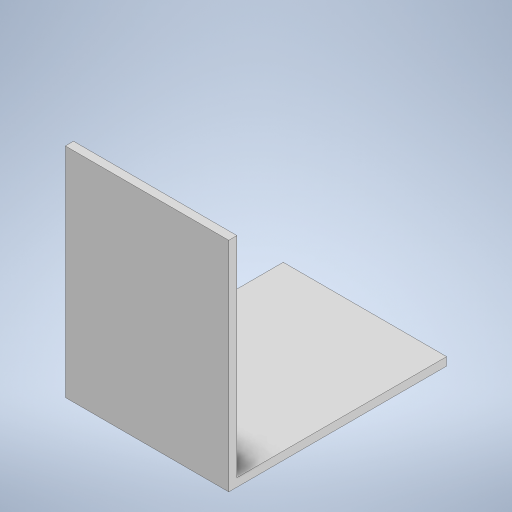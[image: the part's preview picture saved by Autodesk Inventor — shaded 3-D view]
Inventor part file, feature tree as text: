
AUTODESK INVENTOR PART (.ipt)
format: ipt  version: 2023.2 (Build 272271000, 271)  size: 251,392 bytes
history: native  units: mm
features: extrude x2, sketch x2, projected_geometry x1
ambient origin geometry x8: Origin, YZ Plane, XZ Plane, XY Plane, X Axis, Y Axis, Z Axis, Center Point
bodies: Solid1 (feature_tree)
feature tree (5):
  extrude  "Extrusion1"  Depth=60.0mm
  extrude  "Extrusion2"  Depth=80.0mm
  sketch  "Sketch1"  dims[d0=80.0mm d1=60.0mm]
  sketch  "Sketch2"  dims[d2=3.0mm d3=0.0mm d4=80.0mm d5=60.0mm d6=3.0mm d7=0.0mm]
  projected_geometry  "Projected Loop1"
